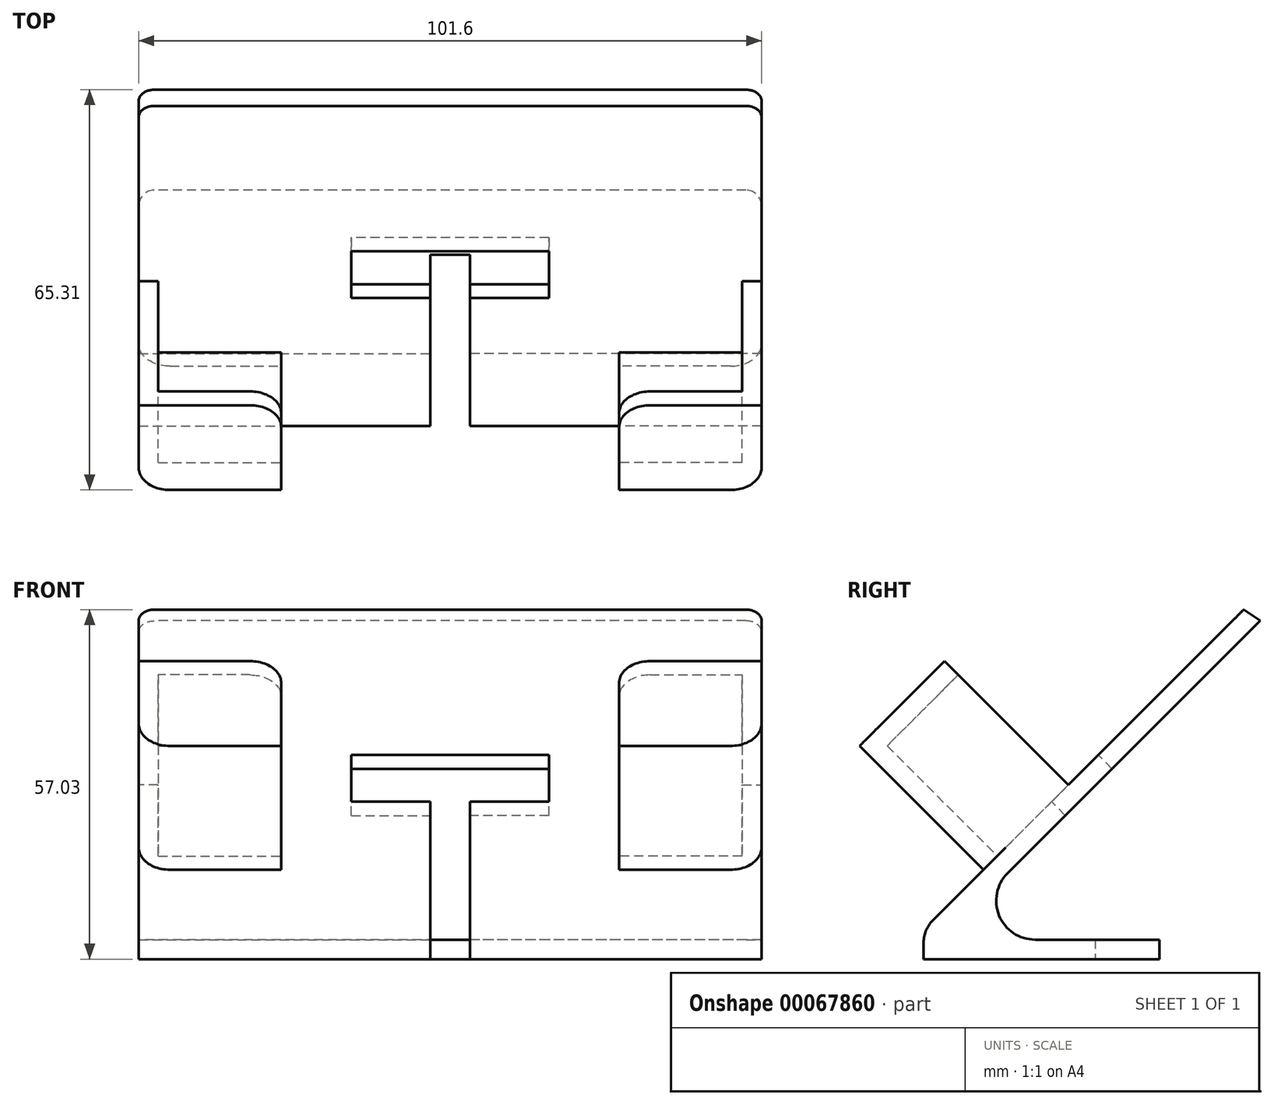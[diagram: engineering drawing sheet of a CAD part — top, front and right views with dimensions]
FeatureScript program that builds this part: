
annotation { "Feature Type Name" : "Feature", "Feature Type Description" : "" }
export const myFeature = defineFeature(function(context is Context, id is Id, definition is map)
    precondition{}
    {
        {
            var Q0;
            Q0=qCreatedBy(makeId("Right.planeOp"),FACE);
            var sketch = newSketch(context, id + "F0", { "sketchPlane" : qUnion([Q0])});
            skLineSegment(sketch, "E0", {"start": v(38.46, 0) * mm, "end": v(0, 0) * mm});
            skLineSegment(sketch, "E1", {"start": v(0, 0) * mm, "end": v(0, 4.81) * mm});
            skPoint(sketch, "E2.visualSharp", {"position": v(0, 0) * mm});
            skLineSegment(sketch, "E3", {"start": v(0, 4.81) * mm, "end": v(52.22, 57.03) * mm});
            skLineSegment(sketch, "E4.0", {"start": v(13.7, 14.02) * mm, "end": v(54.87, 55.2) * mm});
            skLineSegment(sketch, "E4.2", {"start": v(38.46, 3.18) * mm, "end": v(18.18, 3.17) * mm});
            skLineSegment(sketch, "E5", {"start": v(52.22, 57.03) * mm, "end": v(54.87, 55.2) * mm});
            skLineSegment(sketch, "E6", {"start": v(38.46, 3.18) * mm, "end": v(38.46, 0) * mm});
            skPoint(sketch, "E7.visualSharp", {"position": v(2.85, 3.17) * mm});
            skArc(sketch, "E7.filletArc", {"start": v(13.7, 14.02) * mm, "mid": v(12.32, 7.1) * mm, "end": v(18.18, 3.17) * mm});
            skSolve(sketch);
        }
        {
            var Q0;
            Q0 = qSketchRegion(id + "F0", true);
            extrude(context, id + "F1", {"entities" : qUnion([Q0]), "depth" : 50.8 * mm});
        }
        {
            var Q0;
            {var subQ0=makeQuery(id+"F1.opExtrude","SWEPT_FACE",FACE,{"disambiguationData":[OSD([sQuery(id+"F0.wireOp",EDGE,"E3")])]});Q0=makeQuery(id+"F12.boolean.opBoolean","MERGE",FACE,{"derivedFrom":[subQ0,makeQuery(id+"F12.opPattern","COPY",FACE,{"derivedFrom":subQ0,"instanceName":"1"})]});}
            var sketch = newSketch(context, id + "F2", { "sketchPlane" : qUnion([Q0])});
            skLineSegment(sketch, "E8", {"start": v(50.8, 17.22) * mm, "end": v(27.55, 17.22) * mm});
            skLineSegment(sketch, "E9", {"start": v(50.8, 17.22) * mm, "end": v(50.8, 36.77) * mm});
            skLineSegment(sketch, "E10.0", {"start": v(47.63, 20.4) * mm, "end": v(47.63, 36.77) * mm});
            skLineSegment(sketch, "E10.1", {"start": v(47.63, 20.4) * mm, "end": v(27.55, 20.4) * mm});
            skLineSegment(sketch, "E11", {"start": v(47.63, 36.77) * mm, "end": v(50.8, 36.77) * mm});
            skLineSegment(sketch, "E12", {"start": v(27.55, 20.4) * mm, "end": v(27.55, 17.22) * mm});
            skSolve(sketch);
        }
        {
            var Q0;
            Q0 = qSketchRegion(id + "F2", true);
            extrude(context, id + "F3", {"entities" : qUnion([Q0]), "operationType" : NewBodyOperationType.ADD, "depth" : 25.4 * mm});
        }
        {
            var Q0;
            {var subQ0=makeQuery(id+"F1.opExtrude","SWEPT_FACE",FACE,{"disambiguationData":[OSD([sQuery(id+"F0.wireOp",EDGE,"E3")])]});Q0=makeQuery(id+"F12.boolean.opBoolean","MERGE",FACE,{"derivedFrom":[subQ0,makeQuery(id+"F12.opPattern","COPY",FACE,{"derivedFrom":subQ0,"instanceName":"1"})]});}
            var sketch = newSketch(context, id + "F4", { "sketchPlane" : qUnion([Q0])});
            skLineSegment(sketch, "E13.bottom", {"start": v(0, 43.7) * mm, "end": v(16.1, 43.7) * mm});
            skLineSegment(sketch, "E13.top", {"start": v(0, 32.91) * mm, "end": v(16.1, 32.91) * mm});
            skLineSegment(sketch, "E13.left", {"start": v(0, 43.7) * mm, "end": v(0, 32.91) * mm});
            skLineSegment(sketch, "E13.right", {"start": v(16.1, 43.7) * mm, "end": v(16.1, 32.91) * mm});
            skSolve(sketch);
        }
        {
            var Q0;
            Q0 = qSketchRegion(id + "F4", true);
            extrude(context, id + "F5", {"entities" : qUnion([Q0]), "operationType" : NewBodyOperationType.REMOVE, "endBound" : BoundingType.UP_TO_NEXT, "oppositeDirection" : true, "depth" : 25.4 * mm});
        }
        {
            var Q0;
            Q0=qCreatedBy(makeId("Top.planeOp"),FACE);
            var sketch = newSketch(context, id + "F6", { "sketchPlane" : qUnion([Q0])});
            skLineSegment(sketch, "E14.bottom", {"start": v(0, 0) * mm, "end": v(3.24, 0) * mm});
            skLineSegment(sketch, "E14.top", {"start": v(0, 27.97) * mm, "end": v(3.24, 27.97) * mm});
            skLineSegment(sketch, "E14.left", {"start": v(0, 0) * mm, "end": v(0, 27.97) * mm});
            skLineSegment(sketch, "E14.right", {"start": v(3.24, 0) * mm, "end": v(3.24, 27.97) * mm});
            skSolve(sketch);
        }
        {
            var Q0;
            Q0 = qSketchRegion(id + "F6", true);
            var Q1;
            {var subQ0=makeQuery(id+"F5.boolean.opBoolean","COPY",FACE,{"derivedFrom":makeQuery(id+"F5.opExtrude","SWEPT_FACE",FACE,{"disambiguationData":[OSD([sQuery(id+"F4.wireOp",EDGE,"E13.top")])]})});Q1=makeQuery(id+"F12.boolean.opBoolean","MERGE",FACE,{"derivedFrom":[subQ0,makeQuery(id+"F12.opPattern","COPY",FACE,{"derivedFrom":subQ0,"instanceName":"1"})]});}
            extrude(context, id + "F7", {"entities" : qUnion([Q0]), "operationType" : NewBodyOperationType.REMOVE, "endBound" : BoundingType.UP_TO_SURFACE, "endBoundEntityFace" : qUnion([Q1]), "depth" : 25.4 * mm});
        }
        {
            var Q0;
            Q0=makeQuery(id+"F3.opExtrude","CAP_FACE",FACE,{"disambiguationData":[OSD([sQuery(id+"F2.wireOp",EDGE,"E8"),sQuery(id+"F2.wireOp",EDGE,"E9"),sQuery(id+"F2.wireOp",EDGE,"E10.0"),sQuery(id+"F2.wireOp",EDGE,"E10.1"),sQuery(id+"F2.wireOp",EDGE,"E11"),sQuery(id+"F2.wireOp",EDGE,"E12")])],"isStart":false});
            var sketch = newSketch(context, id + "F8", { "sketchPlane" : qUnion([Q0])});
            skLineSegment(sketch, "E15.bottom", {"start": v(50.8, 17.22) * mm, "end": v(27.55, 17.22) * mm});
            skLineSegment(sketch, "E15.top", {"start": v(50.8, 36.77) * mm, "end": v(27.55, 36.77) * mm});
            skLineSegment(sketch, "E15.left", {"start": v(50.8, 17.22) * mm, "end": v(50.8, 36.77) * mm});
            skLineSegment(sketch, "E15.right", {"start": v(27.55, 17.22) * mm, "end": v(27.55, 36.77) * mm});
            skSolve(sketch);
        }
        {
            var Q0;
            Q0 = qSketchRegion(id + "F8", true);
            extrude(context, id + "F9", {"entities" : qUnion([Q0]), "operationType" : NewBodyOperationType.ADD, "depth" : 3.17 * mm});
        }
        {
            var Q0;
            Q0=makeQuery(id+"F1.opExtrude","SWEPT_EDGE",EDGE,{"disambiguationData":[OSD([sQuery(id+"F0.wireOp",EDGE,"E1"),sQuery(id+"F0.wireOp",EDGE,"E3")])]});
            var Q1;
            Q1=makeQuery(id+"F9.boolean.opBoolean","MERGE",EDGE,{"derivedFrom":[makeQuery(id+"F3.opExtrude","SWEPT_EDGE",EDGE,{"disambiguationData":[OSD([sQuery(id+"F0.wireOp",EDGE,"E3"),sQuery(id+"F2.wireOp",EDGE,"E8"),sQuery(id+"F2.wireOp",EDGE,"E9")])]}),makeQuery(id+"F9.opExtrude","SWEPT_EDGE",EDGE,{"disambiguationData":[OSD([sQuery(id+"F8.wireOp",EDGE,"E15.bottom"),sQuery(id+"F8.wireOp",EDGE,"E15.left")])]})]});
            var Q2;
            Q2=makeQuery(id+"F9.opExtrude","SWEPT_EDGE",EDGE,{"disambiguationData":[OSD([sQuery(id+"F8.wireOp",EDGE,"E15.top"),sQuery(id+"F8.wireOp",EDGE,"E15.right")])]});
            fillet(context, id + "F10", {"entities" : qUnion([Q0, Q1, Q2]), "radius" : 5.08 * mm, "tangentPropagation" : true, "allowEdgeOverflow" : false});
        }
        {
            var Q0;
            Q0=makeQuery(id+"F1.opExtrude","CAP_EDGE",EDGE,{"disambiguationData":[OSD([sQuery(id+"F0.wireOp",EDGE,"E5")])],"isStart":false});
            var Q1;
            Q1=makeQuery(id+"F1.opExtrude","CAP_EDGE",EDGE,{"disambiguationData":[OSD([sQuery(id+"F0.wireOp",EDGE,"E6")])],"isStart":false});
            var Q2;
            Q2=makeQuery(id+"F7.boolean.opBoolean","COPY",EDGE,{"derivedFrom":makeQuery(id+"F7.opExtrude","CAP_EDGE",EDGE,{"disambiguationData":[OSD([sQuery(id+"F6.wireOp",EDGE,"E14.right")])],"isStart":false})});
            fillet(context, id + "F11", {"entities" : qUnion([Q0, Q1, Q2]), "radius" : 2.54 * mm, "tangentPropagation" : true, "allowEdgeOverflow" : false});
        }
        {
            var Q0;
            Q0=makeQuery(id+"F1.opExtrude","SWEPT_BODY",BODY,{"disambiguationData":[OSD([sQuery(id+"F0.wireOp",EDGE,"E0"),sQuery(id+"F0.wireOp",EDGE,"E1"),sQuery(id+"F0.wireOp",EDGE,"E3"),sQuery(id+"F0.wireOp",EDGE,"E4.0"),sQuery(id+"F0.wireOp",EDGE,"E4.1"),sQuery(id+"F0.wireOp",EDGE,"E4.2"),sQuery(id+"F0.wireOp",EDGE,"E5"),sQuery(id+"F0.wireOp",EDGE,"E6")])]});
            var Q1;
            Q1=qCreatedBy(makeId("Right.planeOp"),FACE);
            mirror(context, id + "F12", {"operationType" : NewBodyOperationType.ADD, "entities" : qUnion([Q0]), "mirrorPlane" : qUnion([Q1])});
        }
    });
